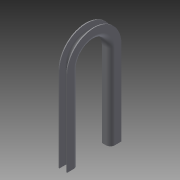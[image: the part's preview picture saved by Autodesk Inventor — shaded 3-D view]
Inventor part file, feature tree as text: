
AUTODESK INVENTOR PART (.ipt)
format: ipt  version: 2015 (Build 190159000, 159)  size: 124,928 bytes
history: native  units: mm
features: sketch x2, sweep x1, fillet x1
ambient origin geometry x8: Origin, YZ Plane, XZ Plane, XY Plane, X Axis, Y Axis, Z Axis, Center Point
bodies: Body1 (feature_tree)
feature tree (4):
  sweep  "Sweep1"
  fillet  "Fillet6"  Radius=6.0mm
  sketch  "Sketch3"  dims[d9=8.0mm d10=1.0mm d11=6.0mm]
  sketch  "Sketch17"  dims[d29=10.0mm d30=6.0mm d49=100.0mm d50=50.0mm d51=50.0mm d52=0.0mm d53=0.0mm d54=5.0mm]
